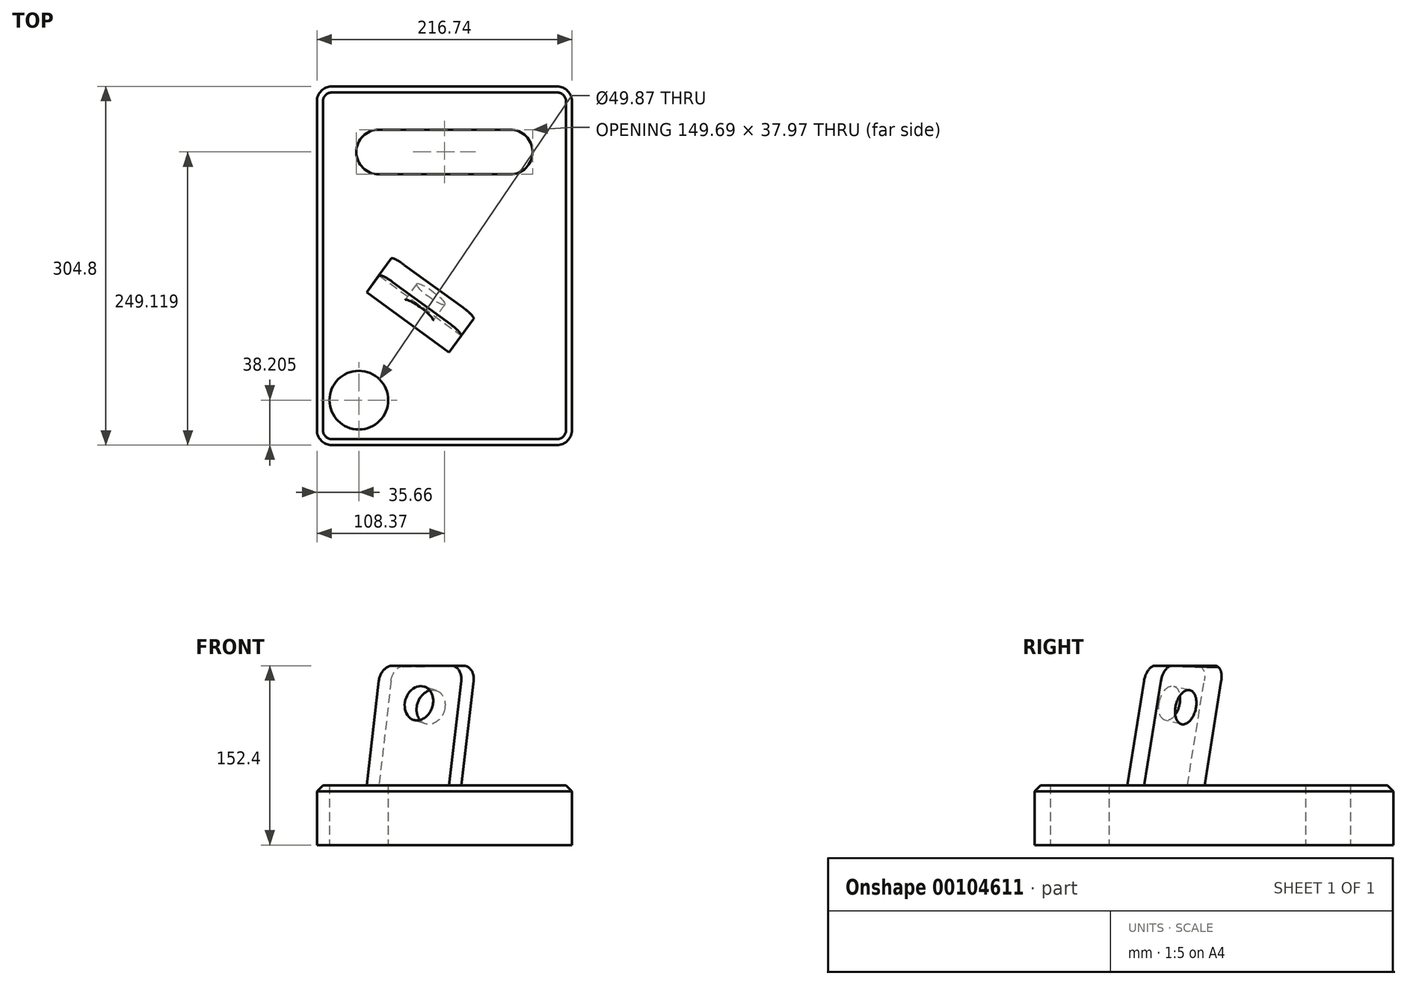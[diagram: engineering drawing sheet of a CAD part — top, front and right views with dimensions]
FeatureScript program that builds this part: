
annotation { "Feature Type Name" : "Feature", "Feature Type Description" : "" }
export const myFeature = defineFeature(function(context is Context, id is Id, definition is map)
    precondition{}
    {
        {
            var Q0;
            Q0=qCreatedBy(makeId("Top.planeOp"),FACE);
            var sketch = newSketch(context, id + "F0", { "sketchPlane" : qUnion([Q0])});
            skLineSegment(sketch, "E0.bottom", {"start": v(108.37, -152.4) * mm, "end": v(-108.37, -152.4) * mm});
            skLineSegment(sketch, "E0.top", {"start": v(108.37, 152.4) * mm, "end": v(-108.37, 152.4) * mm});
            skLineSegment(sketch, "E0.left", {"start": v(108.37, -152.4) * mm, "end": v(108.37, 152.4) * mm});
            skLineSegment(sketch, "E0.right", {"start": v(-108.37, -152.4) * mm, "end": v(-108.37, 152.4) * mm});
            skPoint(sketch, "E0.middle", {"position": v(0, 0) * mm});
            skLineSegment(sketch, "E1.bottom", {"start": v(74.84, 77.73) * mm, "end": v(-74.84, 77.73) * mm});
            skLineSegment(sketch, "E1.top", {"start": v(74.84, 115.7) * mm, "end": v(-74.84, 115.7) * mm});
            skLineSegment(sketch, "E1.left", {"start": v(74.84, 77.73) * mm, "end": v(74.84, 115.7) * mm});
            skLineSegment(sketch, "E1.right", {"start": v(-74.84, 77.73) * mm, "end": v(-74.84, 115.7) * mm});
            skPoint(sketch, "E1.middle", {"position": v(0, 96.72) * mm});
            skCircle(sketch, "E2", {"center": v(-72.71, -114.2) * mm, "radius": 24.93 * mm});
            skSolve(sketch);
        }
        {
            var Q0;
            Q0 = qSketchRegion(id + "F0", true);
            extrude(context, id + "F1", {"entities" : qUnion([Q0]), "depth" : 50.8 * mm});
        }
        {
            var Q0;
            Q0=makeQuery(id+"F1.opExtrude","SWEPT_EDGE",EDGE,{"disambiguationData":[OSD([sQuery(id+"F0.wireOp",EDGE,"E1.top"),sQuery(id+"F0.wireOp",EDGE,"E1.right")])]});
            var Q1;
            Q1=makeQuery(id+"F1.opExtrude","SWEPT_EDGE",EDGE,{"disambiguationData":[OSD([sQuery(id+"F0.wireOp",EDGE,"E1.bottom"),sQuery(id+"F0.wireOp",EDGE,"E1.right")])]});
            var Q2;
            Q2=makeQuery(id+"F1.opExtrude","SWEPT_EDGE",EDGE,{"disambiguationData":[OSD([sQuery(id+"F0.wireOp",EDGE,"E1.bottom"),sQuery(id+"F0.wireOp",EDGE,"E1.left")])]});
            var Q3;
            Q3=makeQuery(id+"F1.opExtrude","SWEPT_EDGE",EDGE,{"disambiguationData":[OSD([sQuery(id+"F0.wireOp",EDGE,"E1.top"),sQuery(id+"F0.wireOp",EDGE,"E1.left")])]});
            fillet(context, id + "F2", {"entities" : qUnion([Q0, Q1, Q2, Q3]), "radius" : 19.05 * mm, "tangentPropagation" : true, "allowEdgeOverflow" : false});
        }
        {
            var Q0;
            Q0=makeQuery(id+"F1.opExtrude","SWEPT_EDGE",EDGE,{"disambiguationData":[OSD([sQuery(id+"F0.wireOp",EDGE,"E0.top"),sQuery(id+"F0.wireOp",EDGE,"E0.left")])]});
            var Q1;
            Q1=makeQuery(id+"F1.opExtrude","SWEPT_EDGE",EDGE,{"disambiguationData":[OSD([sQuery(id+"F0.wireOp",EDGE,"E0.top"),sQuery(id+"F0.wireOp",EDGE,"E0.right")])]});
            var Q2;
            Q2=makeQuery(id+"F1.opExtrude","SWEPT_EDGE",EDGE,{"disambiguationData":[OSD([sQuery(id+"F0.wireOp",EDGE,"E0.bottom"),sQuery(id+"F0.wireOp",EDGE,"E0.right")])]});
            var Q3;
            Q3=makeQuery(id+"F1.opExtrude","SWEPT_EDGE",EDGE,{"disambiguationData":[OSD([sQuery(id+"F0.wireOp",EDGE,"E0.bottom"),sQuery(id+"F0.wireOp",EDGE,"E0.left")])]});
            fillet(context, id + "F3", {"entities" : qUnion([Q0, Q1, Q2, Q3]), "radius" : 12.7 * mm, "tangentPropagation" : true, "allowEdgeOverflow" : false});
        }
        {
            var Q0;
            Q0=makeQuery(id+"F1.opExtrude","CAP_EDGE",EDGE,{"disambiguationData":[OSD([sQuery(id+"F0.wireOp",EDGE,"E0.bottom")])],"isStart":false});
            var Q1;
            Q1=makeQuery(id+"F1.opExtrude","CAP_EDGE",EDGE,{"disambiguationData":[OSD([sQuery(id+"F0.wireOp",EDGE,"E0.left")])],"isStart":false});
            var Q2;
            {var subQ0=sQuery(id+"F0.wireOp",EDGE,"E0.left");var subQ1=sQuery(id+"F0.wireOp",EDGE,"E0.bottom");Q2=makeQuery(id+"F3.opFillet","BLEND_EDGE",EDGE,{"blendedFrom":[makeQuery(id+"F1.opExtrude","SWEPT_EDGE",EDGE,{"disambiguationData":[OSD([subQ1,subQ0])]}),makeQuery(id+"F1.opExtrude","CAP_FACE",FACE,{"disambiguationData":[OSD([subQ1,sQuery(id+"F0.wireOp",EDGE,"E0.top"),subQ0,sQuery(id+"F0.wireOp",EDGE,"E0.right"),sQuery(id+"F0.wireOp",EDGE,"E1.bottom"),sQuery(id+"F0.wireOp",EDGE,"E1.top"),sQuery(id+"F0.wireOp",EDGE,"E1.left"),sQuery(id+"F0.wireOp",EDGE,"E1.right"),sQuery(id+"F0.wireOp",EDGE,"NR31A4xz-r9oS-ccOs-JSWX-FOTRa2rHlJvI")])],"isStart":false})],"blendedInto":[makeQuery(id+"F1.opExtrude","CAP_FACE",FACE,{"disambiguationData":[OSD([subQ1,sQuery(id+"F0.wireOp",EDGE,"E0.top"),subQ0,sQuery(id+"F0.wireOp",EDGE,"E0.right"),sQuery(id+"F0.wireOp",EDGE,"E1.bottom"),sQuery(id+"F0.wireOp",EDGE,"E1.top"),sQuery(id+"F0.wireOp",EDGE,"E1.left"),sQuery(id+"F0.wireOp",EDGE,"E1.right"),sQuery(id+"F0.wireOp",EDGE,"NR31A4xz-r9oS-ccOs-JSWX-FOTRa2rHlJvI")])],"isStart":false})]});}
            var Q3;
            Q3=makeQuery(id+"F1.opExtrude","CAP_EDGE",EDGE,{"disambiguationData":[OSD([sQuery(id+"F0.wireOp",EDGE,"E0.right")])],"isStart":false});
            var Q4;
            {var subQ0=sQuery(id+"F0.wireOp",EDGE,"E0.right");var subQ1=sQuery(id+"F0.wireOp",EDGE,"E0.bottom");Q4=makeQuery(id+"F3.opFillet","BLEND_EDGE",EDGE,{"blendedFrom":[makeQuery(id+"F1.opExtrude","SWEPT_EDGE",EDGE,{"disambiguationData":[OSD([subQ1,subQ0])]}),makeQuery(id+"F1.opExtrude","CAP_FACE",FACE,{"disambiguationData":[OSD([subQ1,sQuery(id+"F0.wireOp",EDGE,"E0.top"),sQuery(id+"F0.wireOp",EDGE,"E0.left"),subQ0,sQuery(id+"F0.wireOp",EDGE,"E1.bottom"),sQuery(id+"F0.wireOp",EDGE,"E1.top"),sQuery(id+"F0.wireOp",EDGE,"E1.left"),sQuery(id+"F0.wireOp",EDGE,"E1.right"),sQuery(id+"F0.wireOp",EDGE,"NR31A4xz-r9oS-ccOs-JSWX-FOTRa2rHlJvI")])],"isStart":false})],"blendedInto":[makeQuery(id+"F1.opExtrude","CAP_FACE",FACE,{"disambiguationData":[OSD([subQ1,sQuery(id+"F0.wireOp",EDGE,"E0.top"),sQuery(id+"F0.wireOp",EDGE,"E0.left"),subQ0,sQuery(id+"F0.wireOp",EDGE,"E1.bottom"),sQuery(id+"F0.wireOp",EDGE,"E1.top"),sQuery(id+"F0.wireOp",EDGE,"E1.left"),sQuery(id+"F0.wireOp",EDGE,"E1.right"),sQuery(id+"F0.wireOp",EDGE,"NR31A4xz-r9oS-ccOs-JSWX-FOTRa2rHlJvI")])],"isStart":false})]});}
            var Q5;
            {var subQ0=sQuery(id+"F0.wireOp",EDGE,"E0.right");var subQ1=sQuery(id+"F0.wireOp",EDGE,"E0.top");Q5=makeQuery(id+"F3.opFillet","BLEND_EDGE",EDGE,{"blendedFrom":[makeQuery(id+"F1.opExtrude","SWEPT_EDGE",EDGE,{"disambiguationData":[OSD([subQ1,subQ0])]}),makeQuery(id+"F1.opExtrude","CAP_FACE",FACE,{"disambiguationData":[OSD([sQuery(id+"F0.wireOp",EDGE,"E0.bottom"),subQ1,sQuery(id+"F0.wireOp",EDGE,"E0.left"),subQ0,sQuery(id+"F0.wireOp",EDGE,"E1.bottom"),sQuery(id+"F0.wireOp",EDGE,"E1.top"),sQuery(id+"F0.wireOp",EDGE,"E1.left"),sQuery(id+"F0.wireOp",EDGE,"E1.right"),sQuery(id+"F0.wireOp",EDGE,"NR31A4xz-r9oS-ccOs-JSWX-FOTRa2rHlJvI")])],"isStart":false})],"blendedInto":[makeQuery(id+"F1.opExtrude","CAP_FACE",FACE,{"disambiguationData":[OSD([sQuery(id+"F0.wireOp",EDGE,"E0.bottom"),subQ1,sQuery(id+"F0.wireOp",EDGE,"E0.left"),subQ0,sQuery(id+"F0.wireOp",EDGE,"E1.bottom"),sQuery(id+"F0.wireOp",EDGE,"E1.top"),sQuery(id+"F0.wireOp",EDGE,"E1.left"),sQuery(id+"F0.wireOp",EDGE,"E1.right"),sQuery(id+"F0.wireOp",EDGE,"NR31A4xz-r9oS-ccOs-JSWX-FOTRa2rHlJvI")])],"isStart":false})]});}
            var Q6;
            Q6=makeQuery(id+"F1.opExtrude","CAP_EDGE",EDGE,{"disambiguationData":[OSD([sQuery(id+"F0.wireOp",EDGE,"E0.top")])],"isStart":false});
            var Q7;
            {var subQ0=sQuery(id+"F0.wireOp",EDGE,"E0.left");var subQ1=sQuery(id+"F0.wireOp",EDGE,"E0.top");Q7=makeQuery(id+"F3.opFillet","BLEND_EDGE",EDGE,{"blendedFrom":[makeQuery(id+"F1.opExtrude","SWEPT_EDGE",EDGE,{"disambiguationData":[OSD([subQ1,subQ0])]}),makeQuery(id+"F1.opExtrude","CAP_FACE",FACE,{"disambiguationData":[OSD([sQuery(id+"F0.wireOp",EDGE,"E0.bottom"),subQ1,subQ0,sQuery(id+"F0.wireOp",EDGE,"E0.right"),sQuery(id+"F0.wireOp",EDGE,"E1.bottom"),sQuery(id+"F0.wireOp",EDGE,"E1.top"),sQuery(id+"F0.wireOp",EDGE,"E1.left"),sQuery(id+"F0.wireOp",EDGE,"E1.right"),sQuery(id+"F0.wireOp",EDGE,"NR31A4xz-r9oS-ccOs-JSWX-FOTRa2rHlJvI")])],"isStart":false})],"blendedInto":[makeQuery(id+"F1.opExtrude","CAP_FACE",FACE,{"disambiguationData":[OSD([sQuery(id+"F0.wireOp",EDGE,"E0.bottom"),subQ1,subQ0,sQuery(id+"F0.wireOp",EDGE,"E0.right"),sQuery(id+"F0.wireOp",EDGE,"E1.bottom"),sQuery(id+"F0.wireOp",EDGE,"E1.top"),sQuery(id+"F0.wireOp",EDGE,"E1.left"),sQuery(id+"F0.wireOp",EDGE,"E1.right"),sQuery(id+"F0.wireOp",EDGE,"NR31A4xz-r9oS-ccOs-JSWX-FOTRa2rHlJvI")])],"isStart":false})]});}
            chamfer(context, id + "F4", {"entities" : qUnion([Q0, Q1, Q2, Q3, Q4, Q5, Q6, Q7]), "width" : 5.08 * mm, "tangentPropagation" : true});
        }
        {
            var Q0;
            Q0=makeQuery(id+"F1.opExtrude","CAP_FACE",FACE,{"disambiguationData":[OSD([sQuery(id+"F0.wireOp",EDGE,"E0.bottom"),sQuery(id+"F0.wireOp",EDGE,"E0.top"),sQuery(id+"F0.wireOp",EDGE,"E0.left"),sQuery(id+"F0.wireOp",EDGE,"E0.right"),sQuery(id+"F0.wireOp",EDGE,"E1.bottom"),sQuery(id+"F0.wireOp",EDGE,"E1.top"),sQuery(id+"F0.wireOp",EDGE,"E1.left"),sQuery(id+"F0.wireOp",EDGE,"E1.right"),sQuery(id+"F0.wireOp",EDGE,"E2")])],"isStart":false});
            var sketch = newSketch(context, id + "F5", { "sketchPlane" : qUnion([Q0])});
            skLineSegment(sketch, "E3", {"start": v(-44.1, 7.9) * mm, "end": v(26.2, -43.12) * mm});
            skLineSegment(sketch, "E4", {"start": v(-88.5, -54.12) * mm, "end": v(-18.5, -104.23) * mm});
            skLineSegment(sketch, "E5", {"start": v(-88.5, -54.12) * mm, "end": v(-44.1, 7.9) * mm});
            skLineSegment(sketch, "E6", {"start": v(-18.5, -104.23) * mm, "end": v(26.2, -43.12) * mm});
            skSolve(sketch);
        }
        {
            var Q0;
            Q0=makeQuery(id+"F5.imprint","IMPRINT",FACE,{"disambiguationData":[TD([[makeQuery(id+"F5.imprint","IMPRINT",EDGE,{"derivedFrom":sQuery(id+"F5.wireOp",EDGE,"E3")}),-1.0]])]});
            extrude(context, id + "F6", {"entities" : qUnion([Q0]), "operationType" : NewBodyOperationType.ADD, "depth" : 101.6 * mm});
        }
        {
            var Q0;
            Q0=makeQuery(id+"F6.opExtrude","SWEPT_FACE",FACE,{"disambiguationData":[OSD([sQuery(id+"F5.wireOp",EDGE,"E6")])]});
            var sketch = newSketch(context, id + "F7", { "sketchPlane" : qUnion([Q0])});
            skLineSegment(sketch, "E7", {"start": v(-37.12, 152.4) * mm, "end": v(-57.2, 50.8) * mm});
            skLineSegment(sketch, "E8", {"start": v(-57.2, 50.8) * mm, "end": v(-39.42, 50.8) * mm});
            skLineSegment(sketch, "E9", {"start": v(-39.42, 50.8) * mm, "end": v(-19.34, 152.4) * mm});
            skLineSegment(sketch, "E10", {"start": v(-19.34, 152.4) * mm, "end": v(-37.12, 152.4) * mm});
            skSolve(sketch);
        }
        {
            var Q0;
            {var subQ0=sQuery(id+"F7.wireOp",EDGE,"E7");Q0=makeQuery(id+"F7.imprint","IMPRINT",FACE,{"disambiguationData":[TD([[makeQuery(id+"F7.imprint","IMPRINT",EDGE,{"derivedFrom":subQ0}),-1.0]])]});}
            var sketch = newSketch(context, id + "F8", { "sketchPlane" : qUnion([Q0])});
            skSolve(sketch);
        }
        {
            var Q0;
            Q0 = qSketchRegion(id + "F8", true);
            var Q1;
            {var subQ0=sQuery(id+"F7.wireOp",EDGE,"E7");Q1=makeQuery(id+"F7.imprint","IMPRINT",FACE,{"disambiguationData":[TD([[makeQuery(id+"F7.imprint","IMPRINT",EDGE,{"derivedFrom":subQ0}),-1.0]])]});}
            var Q2;
            Q2=makeQuery(id+"F6.opExtrude","SWEPT_FACE",FACE,{"disambiguationData":[OSD([sQuery(id+"F5.wireOp",EDGE,"E4")])]});
            var Q3;
            {var subQ0=sQuery(id+"F7.wireOp",EDGE,"E9");Q3=makeQuery(id+"F7.imprint","IMPRINT",FACE,{"disambiguationData":[TD([[makeQuery(id+"F7.imprint","IMPRINT",EDGE,{"derivedFrom":subQ0}),-1.0]])]});}
            extrude(context, id + "F9", {"entities" : qUnion([Q0, Q1, Q2, Q3]), "operationType" : NewBodyOperationType.REMOVE, "oppositeDirection" : true, "depth" : 101.6 * mm});
        }
        {
            var Q0;
            Q0=makeQuery(id+"F6.opExtrude","CAP_EDGE",EDGE,{"disambiguationData":[OSD([sQuery(id+"F5.wireOp",EDGE,"E6")])],"isStart":false});
            var Q1;
            Q1=makeQuery(id+"F6.opExtrude","CAP_EDGE",EDGE,{"disambiguationData":[OSD([sQuery(id+"F5.wireOp",EDGE,"E5")])],"isStart":false});
            fillet(context, id + "F10", {"entities" : qUnion([Q0, Q1]), "radius" : 12.7 * mm, "tangentPropagation" : true, "allowEdgeOverflow" : false});
        }
        {
            var Q0;
            Q0=makeQuery(id+"F9.boolean.opBoolean","COPY",FACE,{"derivedFrom":makeQuery(id+"F9.opExtrude","SWEPT_FACE",FACE,{"disambiguationData":[OSD([sQuery(id+"F7.wireOp",EDGE,"E7")])]})});
            var sketch = newSketch(context, id + "F11", { "sketchPlane" : qUnion([Q0])});
            skCircle(sketch, "E11", {"center": v(20.26, 108.01) * mm, "radius": 14.87 * mm});
            skSolve(sketch);
        }
        {
            var Q0;
            Q0=makeQuery(id+"F11.imprint","IMPRINT",FACE,{"disambiguationData":[TD([[makeQuery(id+"F11.imprint","IMPRINT",EDGE,{"derivedFrom":sQuery(id+"F11.wireOp",EDGE,"E11")}),1.0]])]});
            extrude(context, id + "F12", {"entities" : qUnion([Q0]), "operationType" : NewBodyOperationType.REMOVE, "oppositeDirection" : true, "depth" : 25.4 * mm});
        }
    });
